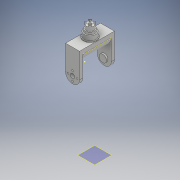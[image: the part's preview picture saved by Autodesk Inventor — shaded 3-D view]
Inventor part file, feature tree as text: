
AUTODESK INVENTOR PART (.ipt)
format: ipt  version: 2018 (Build 220112000, 112)  size: 269,824 bytes
history: native  units: mm
features: extrude x12, sketch x12, plane x4, other x3, fillet x2
ambient origin geometry x8: Origin, YZ Plane, XZ Plane, XY Plane, X Axis, Y Axis, Z Axis, Center Point
bodies: Solid1 (feature_tree)
feature tree (33):
  extrude  "base"  Depth=32.0mm
  plane  "Work Plane1"
  plane  "Work Plane2"
  extrude  "connector_prev_servo"  [1 undecoded]
  fillet  "Fillet3"  Radius=4.0mm
  plane  "Work Plane6"
  extrude  "screw_holes"  Depth=36.0mm TaperAngle=0.0deg
  fillet  "Fillet4"  Radius=9.0mm
  plane  "Work Plane7"
  extrude  "Extrusion14"  Depth=6.0mm
  other  "Edición directa1"
  extrude  "Extrusión30"  Depth=2.0mm TaperAngle=360.0deg
  sketch  "Sketch31"  dims[d79=20.0mm d80=0.0mm d81=9.0mm]
  extrude  "Extrusion31"  Depth=9.0mm
  sketch  "Sketch33"  dims[d154=50.0mm d155=40.0mm d156=40.0mm d157=18.0mm d172=0.0mm d173=0.0mm d174=2.5mm]
  extrude  "Extrusion32"  Depth=6.0mm TaperAngle=0.0deg
  extrude  "Extrusion33"  Depth=2.5mm TaperAngle=0.0deg
  extrude  "Extrusion34"  Depth=9.5mm
  extrude  "Extrusion35"  Depth=10.0mm TaperAngle=0.0deg
  extrude  "Extrusion36"  Depth=16.8mm TaperAngle=0.0deg
  extrude  "Extrusion37"  Depth=2.0mm TaperAngle=0.0deg
  sketch  "Sketch1"  dims[d0=18.0mm d1=32.0mm]
  sketch  "Sketch12"  dims[d2=15.0mm d3=0.0mm d63=-10.0mm d64=4.0mm]
  sketch  "Sketch13"  dims[d65=4.0mm d66=36.0mm d67=0.0mm d71=9.0mm]
  sketch  "Sketch14"  dims[d72=5.5mm d73=6.0mm]
  sketch  "Boceto30"  dims[d74=2.0mm d75=40.0mm d77=360.0deg]
  sketch  "Sketch32"  dims[d82=10.5mm d83=6.0mm d84=0.0mm]
  sketch  "Sketch34"  dims[d175=0.0mm d176=0.0mm d177=-2.5mm d178=9.5mm]
  sketch  "Sketch35"  dims[d179=2.0mm d180=0.0mm d181=10.0mm d182=0.0mm]
  sketch  "Sketch36"  dims[d183=14.8mm d184=16.8mm d185=0.0mm]
  sketch  "Sketch37"  dims[d186=17.0mm d187=1.0mm d188=0.0mm d189=9.7mm d190=20.0mm d191=7.0mm d192=0.0mm d193=20.0mm d194=12.0mm d195=3.0mm d196=0.0mm d197=4.0mm d198=1.0mm d199=0.0mm d200=5.0mm d201=2.5mm d202=12.0mm d203=1.95mm d204=1.95mm d205=40.0mm d207=360.0deg d209=2.0mm d210=0.0mm]
  other  "Desplazar1"
  other  "Desplazar2"
note: 1 required parameter value undecoded (feature->parameter linkage not recoverable at this tier; creation-order binding heuristic only, values carry confidence <= 0.55)
